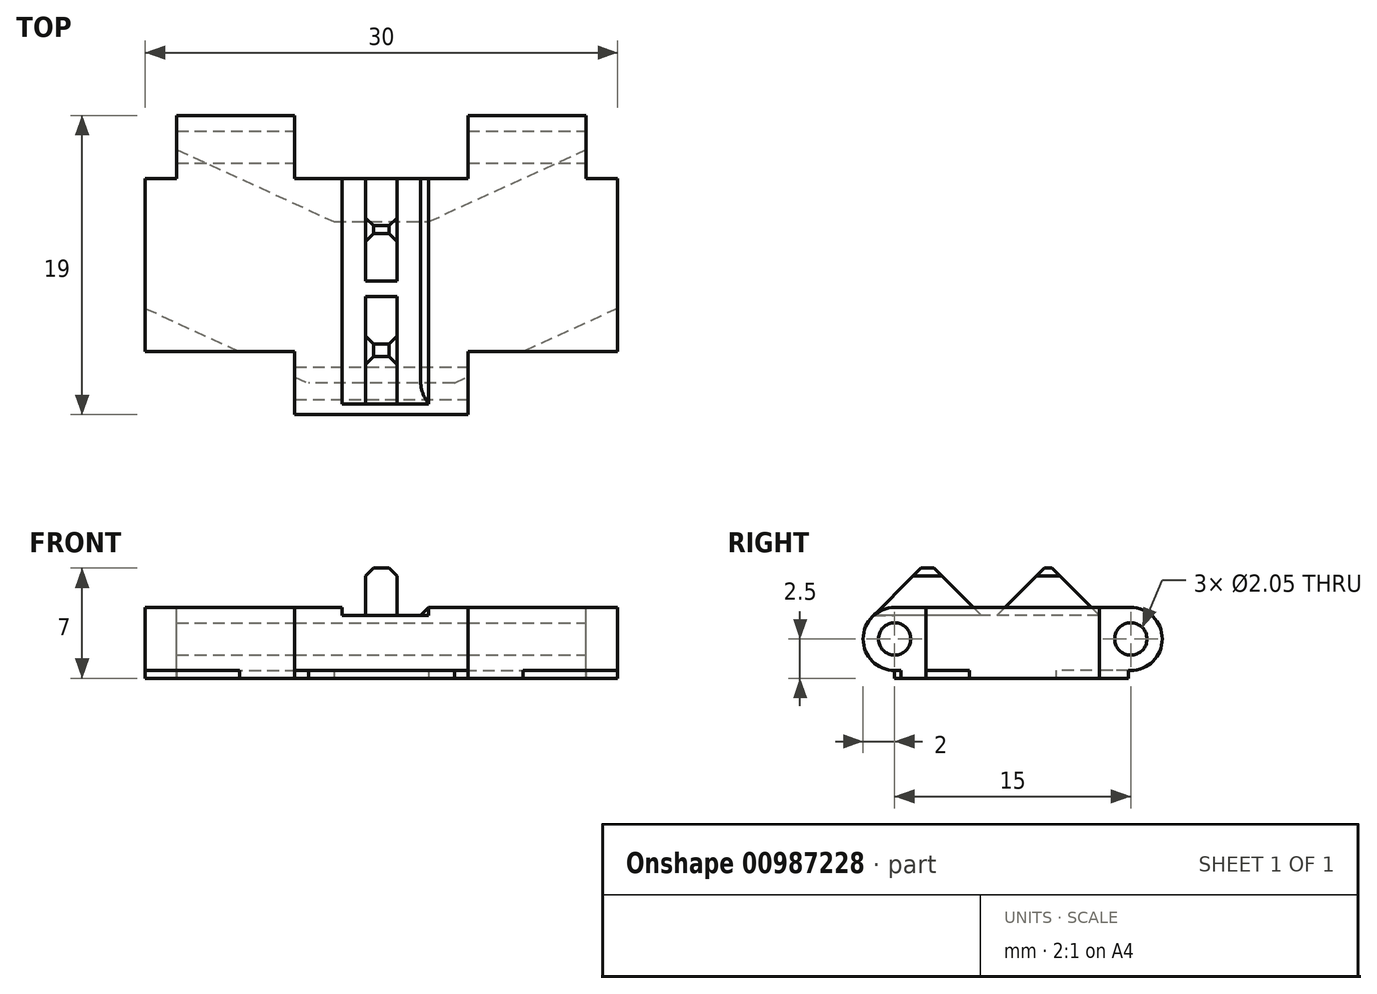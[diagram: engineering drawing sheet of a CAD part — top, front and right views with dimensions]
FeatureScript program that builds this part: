
annotation { "Feature Type Name" : "Feature", "Feature Type Description" : "" }
export const myFeature = defineFeature(function(context is Context, id is Id, definition is map)
    precondition{}
    {
        {
            var Q0;
            Q0=qCreatedBy(makeId("Top.planeOp"),FACE);
            var sketch = newSketch(context, id + "F0", { "sketchPlane" : qUnion([Q0])});
            skLineSegment(sketch, "E0.bottom", {"start": v(15, -7.5) * mm, "end": v(-15, -7.5) * mm});
            skLineSegment(sketch, "E0.top", {"start": v(15, 7.5) * mm, "end": v(-15, 7.5) * mm});
            skLineSegment(sketch, "E0.left", {"start": v(15, -7.5) * mm, "end": v(15, 7.5) * mm});
            skLineSegment(sketch, "E0.right", {"start": v(-15, -7.5) * mm, "end": v(-15, 7.5) * mm});
            skPoint(sketch, "E0.middle", {"position": v(0, 0) * mm});
            skSolve(sketch);
        }
        {
            var Q0;
            Q0=makeQuery(id+"F0.imprint","IMPRINT",FACE,{"disambiguationData":[TD([[makeQuery(id+"F0.imprint","IMPRINT",EDGE,{"derivedFrom":sQuery(id+"F0.wireOp",EDGE,"E0.bottom")}),-1.0]])]});
            extrude(context, id + "F1", {"entities" : qUnion([Q0]), "depth" : 4.5 * mm, "offsetDistance" : 25 * mm});
        }
        {
            var Q0;
            Q0=makeQuery(id+"F1.opExtrude","SWEPT_FACE",FACE,{"disambiguationData":[OSD([sQuery(id+"F0.wireOp",EDGE,"E0.right")])]});
            var sketch = newSketch(context, id + "F2", { "sketchPlane" : qUnion([Q0])});
            skCircle(sketch, "E1", {"center": v(-7.5, 2.5) * mm, "radius": 2 * mm});
            skCircle(sketch, "E2", {"center": v(7.5, 2.5) * mm, "radius": 2 * mm});
            skSolve(sketch);
        }
        {
            var Q0;
            {var subQ0=sQuery(id+"F2.wireOp",EDGE,"vetQoRZT-xKbi-iN1l-QBYZ-xdwohGv9bb5s");var subQ1=sQuery(id+"F0.wireOp",EDGE,"E0.right");var subQ2=makeQuery(id+"F1.opExtrude","SWEPT_EDGE",EDGE,{"disambiguationData":[OSD([sQuery(id+"F0.wireOp",EDGE,"E0.top"),subQ1])]});var subQ3=makeQuery(id+"F2.imprint","INTERSECT",VERTEX,{"disambiguationData":[OD(0.0)],"derivedFrom":[subQ2,subQ0]});Q0=makeQuery(id+"F2.imprint","IMPRINT",FACE,{"disambiguationData":[TD([[makeQuery(id+"F2.imprint","IMPRINT",EDGE,{"disambiguationData":[TD([[subQ3,-1.0]])],"derivedFrom":subQ0}),-1.0]])]});}
            var Q1;
            {var subQ0=sQuery(id+"F2.wireOp",EDGE,"k2q76aXO-4BDj-htHJ-C2at-5MqpkDl38XXc");var subQ1=sQuery(id+"F0.wireOp",EDGE,"E0.right");var subQ2=makeQuery(id+"F1.opExtrude","SWEPT_EDGE",EDGE,{"disambiguationData":[OSD([sQuery(id+"F0.wireOp",EDGE,"E0.bottom"),subQ1])]});var subQ3=makeQuery(id+"F2.imprint","INTERSECT",VERTEX,{"disambiguationData":[OD(0.0)],"derivedFrom":[subQ2,subQ0]});Q1=makeQuery(id+"F2.imprint","IMPRINT",FACE,{"disambiguationData":[TD([[makeQuery(id+"F2.imprint","IMPRINT",EDGE,{"disambiguationData":[TD([[subQ3,1.0]])],"derivedFrom":subQ0}),-1.0]])]});}
            var Q2;
            {var subQ0=sQuery(id+"F2.wireOp",EDGE,"E1");var subQ1=sQuery(id+"F0.wireOp",EDGE,"E0.right");var subQ2=makeQuery(id+"F1.opExtrude","SWEPT_EDGE",EDGE,{"disambiguationData":[OSD([sQuery(id+"F0.wireOp",EDGE,"E0.top"),subQ1])]});var subQ4=makeQuery(id+"F2.imprint","INTERSECT",VERTEX,{"derivedFrom":[subQ2,subQ0]});Q2=makeQuery(id+"F2.imprint","IMPRINT",FACE,{"disambiguationData":[TD([[makeQuery(id+"F2.imprint","IMPRINT",EDGE,{"disambiguationData":[TD([[subQ4,1.0]])],"derivedFrom":subQ0}),1.0]])]});}
            var Q3;
            {var subQ0=sQuery(id+"F2.wireOp",EDGE,"E1");var subQ1=sQuery(id+"F0.wireOp",EDGE,"E0.right");var subQ2=makeQuery(id+"F1.opExtrude","SWEPT_EDGE",EDGE,{"disambiguationData":[OSD([sQuery(id+"F0.wireOp",EDGE,"E0.top"),subQ1])]});var subQ4=makeQuery(id+"F2.imprint","INTERSECT",VERTEX,{"derivedFrom":[subQ2,subQ0]});Q3=makeQuery(id+"F2.imprint","IMPRINT",FACE,{"disambiguationData":[TD([[makeQuery(id+"F2.imprint","IMPRINT",EDGE,{"disambiguationData":[TD([[subQ4,-1.0]])],"derivedFrom":subQ0}),1.0]])]});}
            var Q4;
            {var subQ0=sQuery(id+"F2.wireOp",EDGE,"E2");var subQ1=sQuery(id+"F0.wireOp",EDGE,"E0.right");var subQ2=makeQuery(id+"F1.opExtrude","SWEPT_EDGE",EDGE,{"disambiguationData":[OSD([sQuery(id+"F0.wireOp",EDGE,"E0.bottom"),subQ1])]});var subQ4=makeQuery(id+"F2.imprint","INTERSECT",VERTEX,{"derivedFrom":[subQ2,subQ0]});Q4=makeQuery(id+"F2.imprint","IMPRINT",FACE,{"disambiguationData":[TD([[makeQuery(id+"F2.imprint","IMPRINT",EDGE,{"disambiguationData":[TD([[subQ4,-1.0]])],"derivedFrom":subQ0}),1.0]])]});}
            extrude(context, id + "F3", {"entities" : qUnion([Q0, Q1, Q2, Q3, Q4]), "operationType" : NewBodyOperationType.ADD, "oppositeDirection" : true, "depth" : 30 * mm, "offsetDistance" : 25 * mm});
        }
        {
            var Q0;
            Q0=makeQuery(id+"F1.opExtrude","CAP_FACE",FACE,{"disambiguationData":[OSD([sQuery(id+"F0.wireOp",EDGE,"E0.bottom"),sQuery(id+"F0.wireOp",EDGE,"E0.top"),sQuery(id+"F0.wireOp",EDGE,"E0.left"),sQuery(id+"F0.wireOp",EDGE,"E0.right")])],"isStart":false});
            var sketch = newSketch(context, id + "F4", { "sketchPlane" : qUnion([Q0])});
            skLineSegment(sketch, "E3.bottom", {"start": v(-13, 7.5) * mm, "end": v(-5.5, 7.5) * mm});
            skLineSegment(sketch, "E3.top", {"start": v(-13, 9.5) * mm, "end": v(-5.5, 9.5) * mm});
            skLineSegment(sketch, "E3.left", {"start": v(-13, 7.5) * mm, "end": v(-13, 9.5) * mm});
            skLineSegment(sketch, "E3.right", {"start": v(-5.5, 7.5) * mm, "end": v(-5.5, 9.5) * mm});
            skLineSegment(sketch, "E4.bottom", {"start": v(5.5, 7.5) * mm, "end": v(13, 7.5) * mm});
            skLineSegment(sketch, "E4.top", {"start": v(5.5, 9.5) * mm, "end": v(13, 9.5) * mm});
            skLineSegment(sketch, "E4.left", {"start": v(5.5, 7.5) * mm, "end": v(5.5, 9.5) * mm});
            skLineSegment(sketch, "E4.right", {"start": v(13, 7.5) * mm, "end": v(13, 9.5) * mm});
            skLineSegment(sketch, "E5.bottom", {"start": v(-5.5, -7.5) * mm, "end": v(5.5, -7.5) * mm});
            skLineSegment(sketch, "E5.top", {"start": v(-5.5, -9.5) * mm, "end": v(5.5, -9.5) * mm});
            skLineSegment(sketch, "E5.left", {"start": v(-5.5, -7.5) * mm, "end": v(-5.5, -9.5) * mm});
            skLineSegment(sketch, "E5.right", {"start": v(5.5, -7.5) * mm, "end": v(5.5, -9.5) * mm});
            skLineSegment(sketch, "E6", {"start": v(13, 9.5) * mm, "end": v(15, 9.5) * mm});
            skLineSegment(sketch, "E7", {"start": v(15, 9.5) * mm, "end": v(15, 7.5) * mm});
            skLineSegment(sketch, "E8", {"start": v(15, 7.5) * mm, "end": v(13, 7.5) * mm});
            skLineSegment(sketch, "E9", {"start": v(-13, 9.5) * mm, "end": v(-15, 9.5) * mm});
            skLineSegment(sketch, "E10", {"start": v(-15, 9.5) * mm, "end": v(-15, 7.5) * mm});
            skLineSegment(sketch, "E11", {"start": v(-15, 7.5) * mm, "end": v(-13, 7.5) * mm});
            skLineSegment(sketch, "E12", {"start": v(-5.5, -9.5) * mm, "end": v(-15, -9.5) * mm});
            skLineSegment(sketch, "E13", {"start": v(-15, -9.5) * mm, "end": v(-15, -7.5) * mm});
            skLineSegment(sketch, "E14", {"start": v(-15, -7.5) * mm, "end": v(-5.5, -7.5) * mm});
            skLineSegment(sketch, "E15", {"start": v(5.5, -7.5) * mm, "end": v(15, -7.5) * mm});
            skLineSegment(sketch, "E16", {"start": v(15, -7.5) * mm, "end": v(15, -9.5) * mm});
            skLineSegment(sketch, "E17", {"start": v(15, -9.5) * mm, "end": v(5.5, -9.5) * mm});
            skLineSegment(sketch, "E18", {"start": v(-5.5, 9.5) * mm, "end": v(5.5, 9.5) * mm});
            skSolve(sketch);
        }
        {
            var Q0;
            Q0=makeQuery(id+"F4.imprint","IMPRINT",FACE,{"disambiguationData":[TD([[makeQuery(id+"F4.imprint","IMPRINT",EDGE,{"derivedFrom":sQuery(id+"F4.wireOp",EDGE,"E5.left")}),-1.0]])]});
            var Q1;
            Q1=makeQuery(id+"F4.imprint","IMPRINT",FACE,{"disambiguationData":[TD([[makeQuery(id+"F4.imprint","IMPRINT",EDGE,{"derivedFrom":sQuery(id+"F4.wireOp",EDGE,"E5.right")}),1.0]])]});
            var Q2;
            Q2=makeQuery(id+"F4.imprint","IMPRINT",FACE,{"disambiguationData":[TD([[makeQuery(id+"F4.imprint","IMPRINT",EDGE,{"derivedFrom":sQuery(id+"F4.wireOp",EDGE,"E3.left")}),1.0]])]});
            var Q3;
            Q3=makeQuery(id+"F4.imprint","IMPRINT",FACE,{"disambiguationData":[TD([[makeQuery(id+"F4.imprint","IMPRINT",EDGE,{"derivedFrom":sQuery(id+"F4.wireOp",EDGE,"E4.right")}),-1.0]])]});
            var Q4;
            {var subQ0=sQuery(id+"F4.wireOp",EDGE,"E3.right");Q4=makeQuery(id+"F4.imprint","IMPRINT",FACE,{"disambiguationData":[TD([[makeQuery(id+"F4.imprint","IMPRINT",EDGE,{"derivedFrom":subQ0}),-1.0]])]});}
            extrude(context, id + "F5", {"entities" : qUnion([Q0, Q1, Q2, Q3, Q4]), "operationType" : NewBodyOperationType.REMOVE, "oppositeDirection" : true, "depth" : 25 * mm, "offsetDistance" : 25 * mm});
        }
        {
            var Q0;
            Q0=makeQuery(id+"F3.boolean.opBoolean","MERGE",FACE,{"derivedFrom":[makeQuery(id+"F1.opExtrude","SWEPT_FACE",FACE,{"disambiguationData":[OSD([sQuery(id+"F0.wireOp",EDGE,"E0.left")])]}),makeQuery(id+"F3.opExtrude","CAP_FACE",FACE,{"disambiguationData":[OSD([sQuery(id+"F2.wireOp",EDGE,"E1")])],"isStart":false}),makeQuery(id+"F3.opExtrude","CAP_FACE",FACE,{"disambiguationData":[OSD([sQuery(id+"F0.wireOp",EDGE,"E0.bottom"),sQuery(id+"F0.wireOp",EDGE,"E0.right"),sQuery(id+"F2.wireOp",EDGE,"E2")])],"isStart":false})]});
            var sketch = newSketch(context, id + "F6", { "sketchPlane" : qUnion([Q0])});
            skCircle(sketch, "E19", {"center": v(-7.5, 2.5) * mm, "radius": 1.02 * mm});
            skCircle(sketch, "E20", {"center": v(7.5, 2.5) * mm, "radius": 1.02 * mm});
            skSolve(sketch);
        }
        {
            var Q0;
            Q0=qSketchRegion(id+"F6",true);
            extrude(context, id + "F7", {"entities" : qUnion([Q0]), "operationType" : NewBodyOperationType.REMOVE, "oppositeDirection" : true, "depth" : 30 * mm, "offsetDistance" : 25 * mm});
        }
        {
            var Q0;
            Q0=makeQuery(id+"F1.opExtrude","CAP_FACE",FACE,{"disambiguationData":[OSD([sQuery(id+"F0.wireOp",EDGE,"E0.bottom"),sQuery(id+"F0.wireOp",EDGE,"E0.top"),sQuery(id+"F0.wireOp",EDGE,"E0.left"),sQuery(id+"F0.wireOp",EDGE,"E0.right")])],"isStart":false});
            var sketch = newSketch(context, id + "F8", { "sketchPlane" : qUnion([Q0])});
            skLineSegment(sketch, "E21.bottom", {"start": v(-5.5, -7.5) * mm, "end": v(-15, -7.5) * mm});
            skLineSegment(sketch, "E21.top", {"start": v(-5.5, -5.5) * mm, "end": v(-15, -5.5) * mm});
            skLineSegment(sketch, "E21.left", {"start": v(-5.5, -7.5) * mm, "end": v(-5.5, -5.5) * mm});
            skLineSegment(sketch, "E21.right", {"start": v(-15, -7.5) * mm, "end": v(-15, -5.5) * mm});
            skLineSegment(sketch, "E22.bottom", {"start": v(5.5, -7.5) * mm, "end": v(15, -7.5) * mm});
            skLineSegment(sketch, "E22.top", {"start": v(5.5, -5.5) * mm, "end": v(15, -5.5) * mm});
            skLineSegment(sketch, "E22.left", {"start": v(5.5, -7.5) * mm, "end": v(5.5, -5.5) * mm});
            skLineSegment(sketch, "E22.right", {"start": v(15, -7.5) * mm, "end": v(15, -5.5) * mm});
            skSolve(sketch);
        }
        {
            var Q0;
            Q0=makeQuery(id+"F8.imprint","IMPRINT",FACE,{"disambiguationData":[TD([[makeQuery(id+"F8.imprint","IMPRINT",EDGE,{"derivedFrom":sQuery(id+"F8.wireOp",EDGE,"E21.bottom")}),-1.0]])]});
            var Q1;
            Q1=makeQuery(id+"F8.imprint","IMPRINT",FACE,{"disambiguationData":[TD([[makeQuery(id+"F8.imprint","IMPRINT",EDGE,{"derivedFrom":sQuery(id+"F8.wireOp",EDGE,"E22.bottom")}),-1.0]])]});
            extrude(context, id + "F9", {"entities" : qUnion([Q0, Q1]), "operationType" : NewBodyOperationType.REMOVE, "oppositeDirection" : true, "depth" : 25 * mm, "offsetDistance" : 25 * mm});
        }
        {
            var Q0;
            Q0=makeQuery(id+"F1.opExtrude","CAP_FACE",FACE,{"disambiguationData":[OSD([sQuery(id+"F0.wireOp",EDGE,"E0.bottom"),sQuery(id+"F0.wireOp",EDGE,"E0.top"),sQuery(id+"F0.wireOp",EDGE,"E0.left"),sQuery(id+"F0.wireOp",EDGE,"E0.right")])],"isStart":false});
            var sketch = newSketch(context, id + "F10", { "sketchPlane" : qUnion([Q0])});
            skLineSegment(sketch, "E23.bottom", {"start": v(-5.5, 7.5) * mm, "end": v(5.5, 7.5) * mm});
            skLineSegment(sketch, "E23.top", {"start": v(-5.5, 5.5) * mm, "end": v(5.5, 5.5) * mm});
            skLineSegment(sketch, "E23.left", {"start": v(-5.5, 7.5) * mm, "end": v(-5.5, 5.5) * mm});
            skLineSegment(sketch, "E23.right", {"start": v(5.5, 7.5) * mm, "end": v(5.5, 5.5) * mm});
            skSolve(sketch);
        }
        {
            var Q0;
            Q0=makeQuery(id+"F10.imprint","IMPRINT",FACE,{"disambiguationData":[TD([[makeQuery(id+"F10.imprint","IMPRINT",EDGE,{"derivedFrom":sQuery(id+"F10.wireOp",EDGE,"E23.bottom")}),1.0]])]});
            extrude(context, id + "F11", {"entities" : qUnion([Q0]), "operationType" : NewBodyOperationType.REMOVE, "oppositeDirection" : true, "depth" : 25 * mm, "offsetDistance" : 25 * mm});
        }
        {
            var Q0;
            Q0=makeQuery(id+"F1.opExtrude","CAP_FACE",FACE,{"disambiguationData":[OSD([sQuery(id+"F0.wireOp",EDGE,"E0.bottom"),sQuery(id+"F0.wireOp",EDGE,"E0.top"),sQuery(id+"F0.wireOp",EDGE,"E0.left"),sQuery(id+"F0.wireOp",EDGE,"E0.right")])],"isStart":false});
            var sketch = newSketch(context, id + "F12", { "sketchPlane" : qUnion([Q0])});
            skLineSegment(sketch, "E24.bottom", {"start": v(-13, 7.5) * mm, "end": v(-15, 7.5) * mm});
            skLineSegment(sketch, "E24.top", {"start": v(-13, 5.5) * mm, "end": v(-15, 5.5) * mm});
            skLineSegment(sketch, "E24.left", {"start": v(-13, 7.5) * mm, "end": v(-13, 5.5) * mm});
            skLineSegment(sketch, "E24.right", {"start": v(-15, 7.5) * mm, "end": v(-15, 5.5) * mm});
            skLineSegment(sketch, "E25.bottom", {"start": v(15, 7.5) * mm, "end": v(13, 7.5) * mm});
            skLineSegment(sketch, "E25.top", {"start": v(15, 5.5) * mm, "end": v(13, 5.5) * mm});
            skLineSegment(sketch, "E25.left", {"start": v(15, 7.5) * mm, "end": v(15, 5.5) * mm});
            skLineSegment(sketch, "E25.right", {"start": v(13, 7.5) * mm, "end": v(13, 5.5) * mm});
            skSolve(sketch);
        }
        {
            var Q0;
            Q0=makeQuery(id+"F12.imprint","IMPRINT",FACE,{"disambiguationData":[TD([[makeQuery(id+"F12.imprint","IMPRINT",EDGE,{"derivedFrom":sQuery(id+"F12.wireOp",EDGE,"E24.bottom")}),1.0]])]});
            var Q1;
            Q1=makeQuery(id+"F12.imprint","IMPRINT",FACE,{"disambiguationData":[TD([[makeQuery(id+"F12.imprint","IMPRINT",EDGE,{"derivedFrom":sQuery(id+"F12.wireOp",EDGE,"E25.bottom")}),1.0]])]});
            extrude(context, id + "F13", {"entities" : qUnion([Q0, Q1]), "operationType" : NewBodyOperationType.REMOVE, "oppositeDirection" : true, "depth" : 25 * mm, "offsetDistance" : 25 * mm});
        }
        {
            var Q0;
            Q0=makeQuery(id+"F1.opExtrude","CAP_FACE",FACE,{"disambiguationData":[OSD([sQuery(id+"F0.wireOp",EDGE,"E0.bottom"),sQuery(id+"F0.wireOp",EDGE,"E0.top"),sQuery(id+"F0.wireOp",EDGE,"E0.left"),sQuery(id+"F0.wireOp",EDGE,"E0.right")])],"isStart":true});
            var sketch = newSketch(context, id + "F14", { "sketchPlane" : qUnion([Q0])});
            skLineSegment(sketch, "E26", {"start": v(0, 5.5) * mm, "end": v(-3, 5.5) * mm});
            skLineSegment(sketch, "E27", {"start": v(-3, 5.5) * mm, "end": v(0, 5.5) * mm});
            skLineSegment(sketch, "E28", {"start": v(0, 5.5) * mm, "end": v(3, 5.5) * mm});
            skLineSegment(sketch, "E29", {"start": v(3, 5.5) * mm, "end": v(15, 0) * mm});
            skLineSegment(sketch, "E30", {"start": v(-15, 0) * mm, "end": v(-3, 5.5) * mm});
            skLineSegment(sketch, "E31", {"start": v(-15, -5.5) * mm, "end": v(-3, 0) * mm});
            skLineSegment(sketch, "E32", {"start": v(-3, 0) * mm, "end": v(3, 0) * mm});
            skLineSegment(sketch, "E33", {"start": v(3, 0) * mm, "end": v(15, -5.5) * mm});
            skLineSegment(sketch, "E34", {"start": v(-15, 2.75) * mm, "end": v(-9, 5.5) * mm});
            skPoint(sketch, "E35.startSnap0", {"position": v(9, 2.75) * mm});
            skLineSegment(sketch, "E36", {"start": v(15, 2.75) * mm, "end": v(9, 5.5) * mm});
            skLineSegment(sketch, "E37", {"start": v(-15, -8.25) * mm, "end": v(-3, -2.75) * mm});
            skLineSegment(sketch, "E38", {"start": v(-3, -2.75) * mm, "end": v(3, -2.75) * mm});
            skLineSegment(sketch, "E39", {"start": v(3, -2.75) * mm, "end": v(15, -8.25) * mm});
            skLineSegment(sketch, "E40", {"start": v(-9, 5.5) * mm, "end": v(-3, 8.25) * mm});
            skLineSegment(sketch, "E41", {"start": v(-3, 8.25) * mm, "end": v(3, 8.25) * mm});
            skLineSegment(sketch, "E42", {"start": v(3, 8.25) * mm, "end": v(9, 5.5) * mm});
            skSolve(sketch);
        }
        {
            var Q0;
            Q0=makeQuery(id+"F14.imprint","IMPRINT",FACE,{"disambiguationData":[TD([[makeQuery(id+"F14.imprint","IMPRINT",EDGE,{"derivedFrom":sQuery(id+"F14.wireOp",EDGE,"E27")}),-1.0]])]});
            var Q1;
            {var subQ0=sQuery(id+"F14.wireOp",EDGE,"E34");Q1=makeQuery(id+"F14.imprint","IMPRINT",FACE,{"disambiguationData":[TD([[makeQuery(id+"F14.imprint","IMPRINT",EDGE,{"derivedFrom":subQ0}),1.0]])]});}
            var Q2;
            {var subQ0=sQuery(id+"F14.wireOp",EDGE,"E36");Q2=makeQuery(id+"F14.imprint","IMPRINT",FACE,{"disambiguationData":[TD([[makeQuery(id+"F14.imprint","IMPRINT",EDGE,{"derivedFrom":subQ0}),-1.0]])]});}
            var Q3;
            {var subQ1=sQuery(id+"F14.wireOp",EDGE,"E38");Q3=makeQuery(id+"F14.imprint","IMPRINT",FACE,{"disambiguationData":[TD([[makeQuery(id+"F14.imprint","IMPRINT",EDGE,{"derivedFrom":subQ1}),-1.0]])]});}
            var Q4;
            {var subQ0=sQuery(id+"F14.wireOp",EDGE,"E40");var subQ3=makeQuery(id+"F5.boolean.opBoolean","INTERSECT",EDGE,{"derivedFrom":[makeQuery(id+"F5.opExtrude","SWEPT_FACE",FACE,{"disambiguationData":[OSD([sQuery(id+"F4.wireOp",EDGE,"E14")])]}),makeQuery(id+"F5.opExtrude","SWEPT_FACE",FACE,{"disambiguationData":[OSD([sQuery(id+"F4.wireOp",EDGE,"E15")])]})]});var subQ4=makeQuery(id+"F14.imprint","INTERSECT",VERTEX,{"derivedFrom":[subQ3,subQ0]});Q4=makeQuery(id+"F14.imprint","IMPRINT",FACE,{"disambiguationData":[TD([[makeQuery(id+"F14.imprint","IMPRINT",EDGE,{"disambiguationData":[TD([[subQ4,1.0]])],"derivedFrom":subQ0}),1.0]])]});}
            var Q5;
            {var subQ0=sQuery(id+"F14.wireOp",EDGE,"E42");var subQ1=makeQuery(id+"F5.boolean.opBoolean","INTERSECT",EDGE,{"derivedFrom":[makeQuery(id+"F5.opExtrude","SWEPT_FACE",FACE,{"disambiguationData":[OSD([sQuery(id+"F4.wireOp",EDGE,"E14")])]}),makeQuery(id+"F5.opExtrude","SWEPT_FACE",FACE,{"disambiguationData":[OSD([sQuery(id+"F4.wireOp",EDGE,"E15")])]})]});var subQ2=makeQuery(id+"F14.imprint","INTERSECT",VERTEX,{"derivedFrom":[subQ1,subQ0]});Q5=makeQuery(id+"F14.imprint","IMPRINT",FACE,{"disambiguationData":[TD([[makeQuery(id+"F14.imprint","IMPRINT",EDGE,{"disambiguationData":[TD([[subQ2,-1.0]])],"derivedFrom":subQ0}),1.0]])]});}
            extrude(context, id + "F15", {"entities" : qUnion([Q0, Q1, Q2, Q3, Q4, Q5]), "operationType" : NewBodyOperationType.REMOVE, "oppositeDirection" : true, "depth" : 0.5 * mm, "offsetDistance" : 25 * mm});
        }
        {
            var Q0;
            Q0=makeQuery(id+"F1.opExtrude","CAP_FACE",FACE,{"disambiguationData":[OSD([sQuery(id+"F0.wireOp",EDGE,"E0.bottom"),sQuery(id+"F0.wireOp",EDGE,"E0.top"),sQuery(id+"F0.wireOp",EDGE,"E0.left"),sQuery(id+"F0.wireOp",EDGE,"E0.right")])],"isStart":false});
            var sketch = newSketch(context, id + "F16", { "sketchPlane" : qUnion([Q0])});
            skLineSegment(sketch, "E43.bottom", {"start": v(-2.5, 5.5) * mm, "end": v(2.5, 5.5) * mm});
            skLineSegment(sketch, "E43.left", {"start": v(-2.5, 5.5) * mm, "end": v(-2.5, -7.5) * mm});
            skLineSegment(sketch, "E43.right", {"start": v(2.5, 5.5) * mm, "end": v(2.5, -7.5) * mm});
            skLineSegment(sketch, "E44", {"start": v(-2.5, -7.5) * mm, "end": v(-2.5, -11.32) * mm});
            skLineSegment(sketch, "E45", {"start": v(-2.5, -11.32) * mm, "end": v(2.5, -11.32) * mm});
            skLineSegment(sketch, "E46", {"start": v(2.5, -11.32) * mm, "end": v(2.5, -7.5) * mm});
            skSolve(sketch);
        }
        {
            var Q0;
            Q0=makeQuery(id+"F16.imprint","IMPRINT",FACE,{"disambiguationData":[TD([[makeQuery(id+"F16.imprint","IMPRINT",EDGE,{"derivedFrom":sQuery(id+"F16.wireOp",EDGE,"E43.bottom")}),-1.0]])]});
            var Q1;
            {var subQ0=sQuery(id+"F16.wireOp",EDGE,"E44");Q1=makeQuery(id+"F16.imprint","IMPRINT",FACE,{"disambiguationData":[TD([[makeQuery(id+"F16.imprint","IMPRINT",EDGE,{"derivedFrom":subQ0}),1.0]])]});}
            extrude(context, id + "F17", {"entities" : qUnion([Q0, Q1]), "operationType" : NewBodyOperationType.REMOVE, "oppositeDirection" : true, "depth" : 0.5 * mm, "offsetDistance" : 25 * mm});
        }
        {
            var Q0;
            Q0=makeQuery(id+"F17.boolean.opBoolean","COPY",FACE,{"derivedFrom":makeQuery(id+"F17.opExtrude","CAP_FACE",FACE,{"disambiguationData":[OSD([sQuery(id+"F16.wireOp",EDGE,"E43.bottom"),sQuery(id+"F16.wireOp",EDGE,"E43.left"),sQuery(id+"F16.wireOp",EDGE,"E43.right"),sQuery(id+"F16.wireOp",EDGE,"E44"),sQuery(id+"F16.wireOp",EDGE,"E45"),sQuery(id+"F16.wireOp",EDGE,"E46")])],"isStart":false})});
            var sketch = newSketch(context, id + "F18", { "sketchPlane" : qUnion([Q0])});
            skLineSegment(sketch, "E47.bottom", {"start": v(-1, 5.5) * mm, "end": v(1, 5.5) * mm});
            skLineSegment(sketch, "E47.top", {"start": v(-1, -8.82) * mm, "end": v(1, -8.82) * mm});
            skLineSegment(sketch, "E47.left", {"start": v(-1, 5.5) * mm, "end": v(-1, -8.82) * mm});
            skLineSegment(sketch, "E47.right", {"start": v(1, 5.5) * mm, "end": v(1, -8.82) * mm});
            skSolve(sketch);
        }
        {
            var Q0;
            Q0=makeQuery(id+"F18.imprint","IMPRINT",FACE,{"disambiguationData":[TD([[makeQuery(id+"F18.imprint","IMPRINT",EDGE,{"derivedFrom":sQuery(id+"F18.wireOp",EDGE,"E47.bottom")}),-1.0]])]});
            extrude(context, id + "F19", {"entities" : qUnion([Q0]), "operationType" : NewBodyOperationType.ADD, "depth" : 3 * mm, "offsetDistance" : 25 * mm});
        }
        {
            var Q0;
            Q0=makeQuery(id+"F19.opExtrude","CAP_EDGE",EDGE,{"disambiguationData":[OSD([sQuery(id+"F18.wireOp",EDGE,"E47.top")])],"isStart":false});
            chamfer(context, id + "F20", {"entities" : qUnion([Q0]), "width" : 3 * mm, "tangentPropagation" : true});
        }
        {
            var Q0;
            Q0=makeQuery(id+"F19.opExtrude","CAP_EDGE",EDGE,{"disambiguationData":[OSD([sQuery(id+"F18.wireOp",EDGE,"E47.bottom")])],"isStart":false});
            chamfer(context, id + "F21", {"entities" : qUnion([Q0]), "width" : 3 * mm, "tangentPropagation" : true});
        }
        {
            var Q0;
            Q0=makeQuery(id+"F19.opExtrude","CAP_EDGE",EDGE,{"disambiguationData":[OSD([sQuery(id+"F18.wireOp",EDGE,"E47.left")])],"isStart":false});
            var Q1;
            Q1=makeQuery(id+"F19.opExtrude","CAP_EDGE",EDGE,{"disambiguationData":[OSD([sQuery(id+"F18.wireOp",EDGE,"E47.right")])],"isStart":false});
            chamfer(context, id + "F22", {"entities" : qUnion([Q0, Q1]), "width" : 0.5 * mm, "tangentPropagation" : true});
        }
        {
            var Q0;
            Q0=makeQuery(id+"F17.boolean.opBoolean","COPY",EDGE,{"derivedFrom":makeQuery(id+"F17.opExtrude","CAP_EDGE",EDGE,{"disambiguationData":[OSD([sQuery(id+"F16.wireOp",EDGE,"E43.right"),sQuery(id+"F16.wireOp",EDGE,"E46")])],"isStart":true})});
            var Q1;
            Q1=makeQuery(id+"F17.boolean.opBoolean","COPY",EDGE,{"derivedFrom":makeQuery(id+"F17.opExtrude","CAP_EDGE",EDGE,{"disambiguationData":[OSD([sQuery(id+"F16.wireOp",EDGE,"E43.left"),sQuery(id+"F16.wireOp",EDGE,"E44")])],"isStart":true})});
            chamfer(context, id + "F23", {"entities" : qUnion([Q0, Q1]), "width" : 0.5 * mm, "tangentPropagation" : true});
        }
        {
            var Q0;
            Q0=makeQuery(id+"F19.opExtrude","SWEPT_FACE",FACE,{"disambiguationData":[OSD([sQuery(id+"F18.wireOp",EDGE,"E47.right")])]});
            var sketch = newSketch(context, id + "F24", { "sketchPlane" : qUnion([Q0])});
            skLineSegment(sketch, "E48", {"start": v(-2, 4) * mm, "end": v(-5, 7) * mm});
            skLineSegment(sketch, "E49", {"start": v(-1, 4) * mm, "end": v(2, 7) * mm});
            skLineSegment(sketch, "E50", {"start": v(-1.5, 4) * mm, "end": v(-11.38, 4) * mm});
            skLineSegment(sketch, "E51", {"start": v(-5, 7) * mm, "end": v(2, 7) * mm});
            skLineSegment(sketch, "E52", {"start": v(-2, 4) * mm, "end": v(-1, 4) * mm});
            skSolve(sketch);
        }
        {
            var Q0;
            {var subQ0=sQuery(id+"F24.wireOp",EDGE,"E51");Q0=makeQuery(id+"F24.imprint","IMPRINT",FACE,{"disambiguationData":[TD([[makeQuery(id+"F24.imprint","IMPRINT",EDGE,{"derivedFrom":subQ0}),-1.0]])]});}
            var Q1;
            {var subQ1=sQuery(id+"F24.wireOp",EDGE,"E48");var subQ2=sQuery(id+"F18.wireOp",EDGE,"E47.right");var subQ4=makeQuery(id+"F22.opChamfer","BLEND_EDGE",EDGE,{"blendedFrom":[makeQuery(id+"F19.opExtrude","CAP_EDGE",EDGE,{"disambiguationData":[OSD([subQ2])],"isStart":false}),makeQuery(id+"F19.opExtrude","SWEPT_FACE",FACE,{"disambiguationData":[OSD([subQ2])]})],"blendedInto":[makeQuery(id+"F19.opExtrude","SWEPT_FACE",FACE,{"disambiguationData":[OSD([subQ2])]})]});var subQ5=makeQuery(id+"F24.imprint","INTERSECT",VERTEX,{"derivedFrom":[subQ4,subQ1]});Q1=makeQuery(id+"F24.imprint","IMPRINT",FACE,{"disambiguationData":[TD([[makeQuery(id+"F24.imprint","IMPRINT",EDGE,{"disambiguationData":[TD([[subQ5,1.0]])],"derivedFrom":subQ1}),-1.0]])]});}
            extrude(context, id + "F25", {"entities" : qUnion([Q0, Q1]), "operationType" : NewBodyOperationType.REMOVE, "oppositeDirection" : true, "depth" : 3 * mm, "offsetDistance" : 25 * mm});
        }
    });
